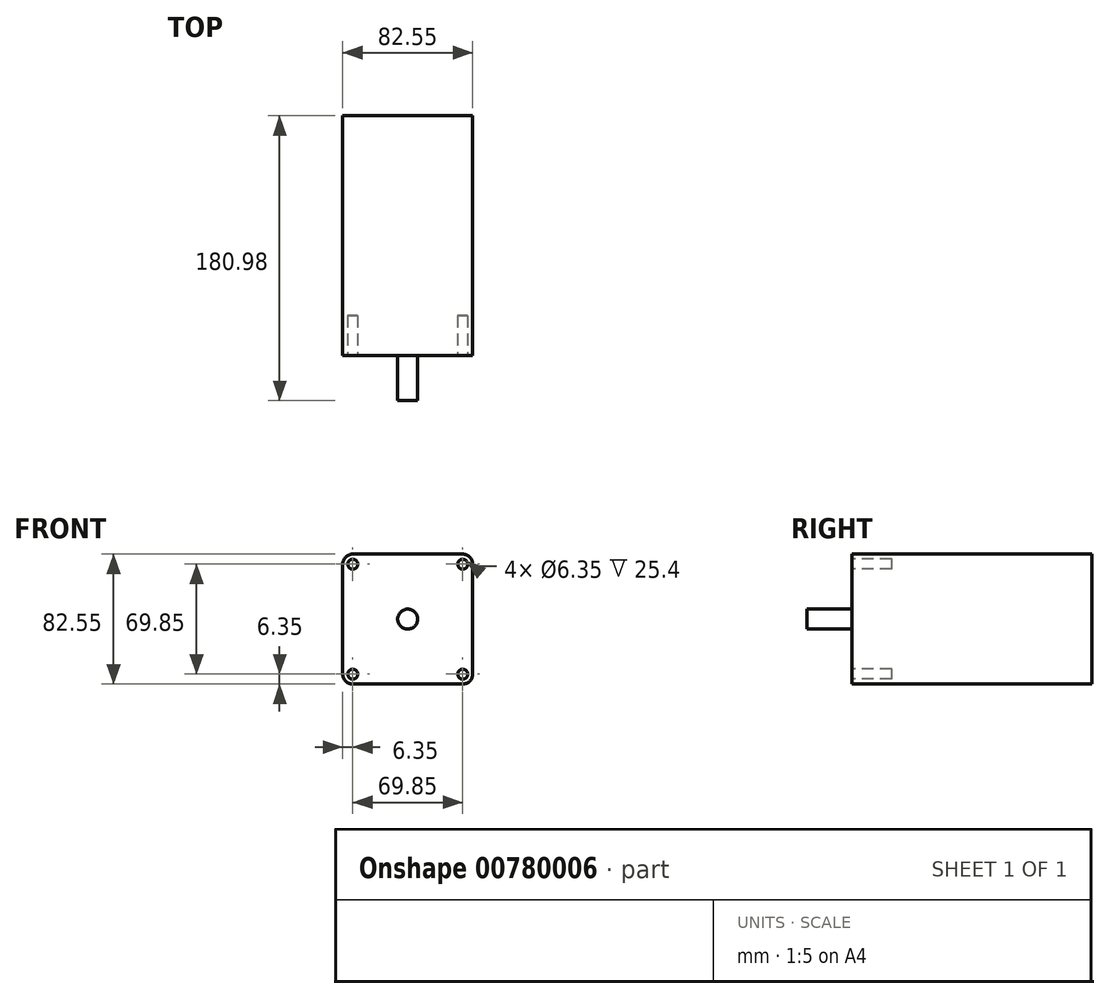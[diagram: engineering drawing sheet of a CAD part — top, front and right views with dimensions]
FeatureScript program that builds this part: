
annotation { "Feature Type Name" : "Feature", "Feature Type Description" : "" }
export const myFeature = defineFeature(function(context is Context, id is Id, definition is map)
    precondition{}
    {
        {
            var Q0;
            Q0=qCreatedBy(makeId("Front.planeOp"),FACE);
            var sketch = newSketch(context, id + "F0", { "sketchPlane" : qUnion([Q0])});
            skLineSegment(sketch, "E0.bottom", {"start": v(0, 0) * mm, "end": v(82.55, 0) * mm});
            skLineSegment(sketch, "E0.top", {"start": v(0, 82.55) * mm, "end": v(82.55, 82.55) * mm});
            skLineSegment(sketch, "E0.left", {"start": v(0, 0) * mm, "end": v(0, 82.55) * mm});
            skLineSegment(sketch, "E0.right", {"start": v(82.55, 0) * mm, "end": v(82.55, 82.55) * mm});
            skSolve(sketch);
        }
        {
            var Q0;
            Q0 = qSketchRegion(id + "F0", true);
            extrude(context, id + "F1", {"entities" : qUnion([Q0]), "depth" : 152.4 * mm, "offsetDistance" : 25.4 * mm});
        }
        {
            var Q0;
            Q0=makeQuery(id+"F1.opExtrude","SWEPT_EDGE",EDGE,{"disambiguationData":[OSD([sQuery(id+"F0.wireOp",EDGE,"E0.top"),sQuery(id+"F0.wireOp",EDGE,"E0.left")])]});
            var Q1;
            Q1=makeQuery(id+"F1.opExtrude","SWEPT_EDGE",EDGE,{"disambiguationData":[OSD([sQuery(id+"F0.wireOp",EDGE,"E0.bottom"),sQuery(id+"F0.wireOp",EDGE,"E0.left")])]});
            var Q2;
            Q2=makeQuery(id+"F1.opExtrude","SWEPT_EDGE",EDGE,{"disambiguationData":[OSD([sQuery(id+"F0.wireOp",EDGE,"E0.top"),sQuery(id+"F0.wireOp",EDGE,"E0.right")])]});
            var Q3;
            Q3=makeQuery(id+"F1.opExtrude","SWEPT_EDGE",EDGE,{"disambiguationData":[OSD([sQuery(id+"F0.wireOp",EDGE,"E0.bottom"),sQuery(id+"F0.wireOp",EDGE,"E0.right")])]});
            fillet(context, id + "F2", {"entities" : qUnion([Q0, Q1, Q2, Q3]), "radius" : 6.35 * mm, "tangentPropagation" : true, "allowEdgeOverflow" : false});
        }
        {
            var Q0;
            Q0=makeQuery(id+"F1.opExtrude","CAP_FACE",FACE,{"disambiguationData":[OSD([sQuery(id+"F0.wireOp",EDGE,"E0.bottom"),sQuery(id+"F0.wireOp",EDGE,"E0.top"),sQuery(id+"F0.wireOp",EDGE,"E0.left"),sQuery(id+"F0.wireOp",EDGE,"E0.right")])],"isStart":false});
            var sketch = newSketch(context, id + "F3", { "sketchPlane" : qUnion([Q0])});
            skCircle(sketch, "E1", {"center": v(41.27, 41.28) * mm, "radius": 6.35 * mm});
            skPoint(sketch, "E1.centerSnap0", {"position": v(41.27, 82.55) * mm});
            skPoint(sketch, "E1.centerSnap1", {"position": v(0, 41.28) * mm});
            skSolve(sketch);
        }
        {
            var Q0;
            Q0 = qSketchRegion(id + "F3", true);
            extrude(context, id + "F4", {"entities" : qUnion([Q0]), "operationType" : NewBodyOperationType.ADD, "depth" : 28.57 * mm, "offsetDistance" : 25.4 * mm});
        }
        {
            var Q0;
            Q0=makeQuery(id+"F1.opExtrude","CAP_FACE",FACE,{"disambiguationData":[OSD([sQuery(id+"F0.wireOp",EDGE,"E0.bottom"),sQuery(id+"F0.wireOp",EDGE,"E0.top"),sQuery(id+"F0.wireOp",EDGE,"E0.left"),sQuery(id+"F0.wireOp",EDGE,"E0.right")])],"isStart":false});
            var sketch = newSketch(context, id + "F5", { "sketchPlane" : qUnion([Q0])});
            skCircle(sketch, "E2", {"center": v(6.35, 76.2) * mm, "radius": 3.18 * mm});
            skCircle(sketch, "E3", {"center": v(6.35, 6.35) * mm, "radius": 3.18 * mm});
            skCircle(sketch, "E4", {"center": v(76.2, 76.2) * mm, "radius": 3.18 * mm});
            skCircle(sketch, "E5", {"center": v(76.2, 6.35) * mm, "radius": 3.18 * mm});
            skSolve(sketch);
        }
        {
            var Q0;
            Q0 = qSketchRegion(id + "F5", true);
            extrude(context, id + "F6", {"entities" : qUnion([Q0]), "operationType" : NewBodyOperationType.REMOVE, "oppositeDirection" : true, "depth" : 25.4 * mm, "offsetDistance" : 25.4 * mm});
        }
    });
